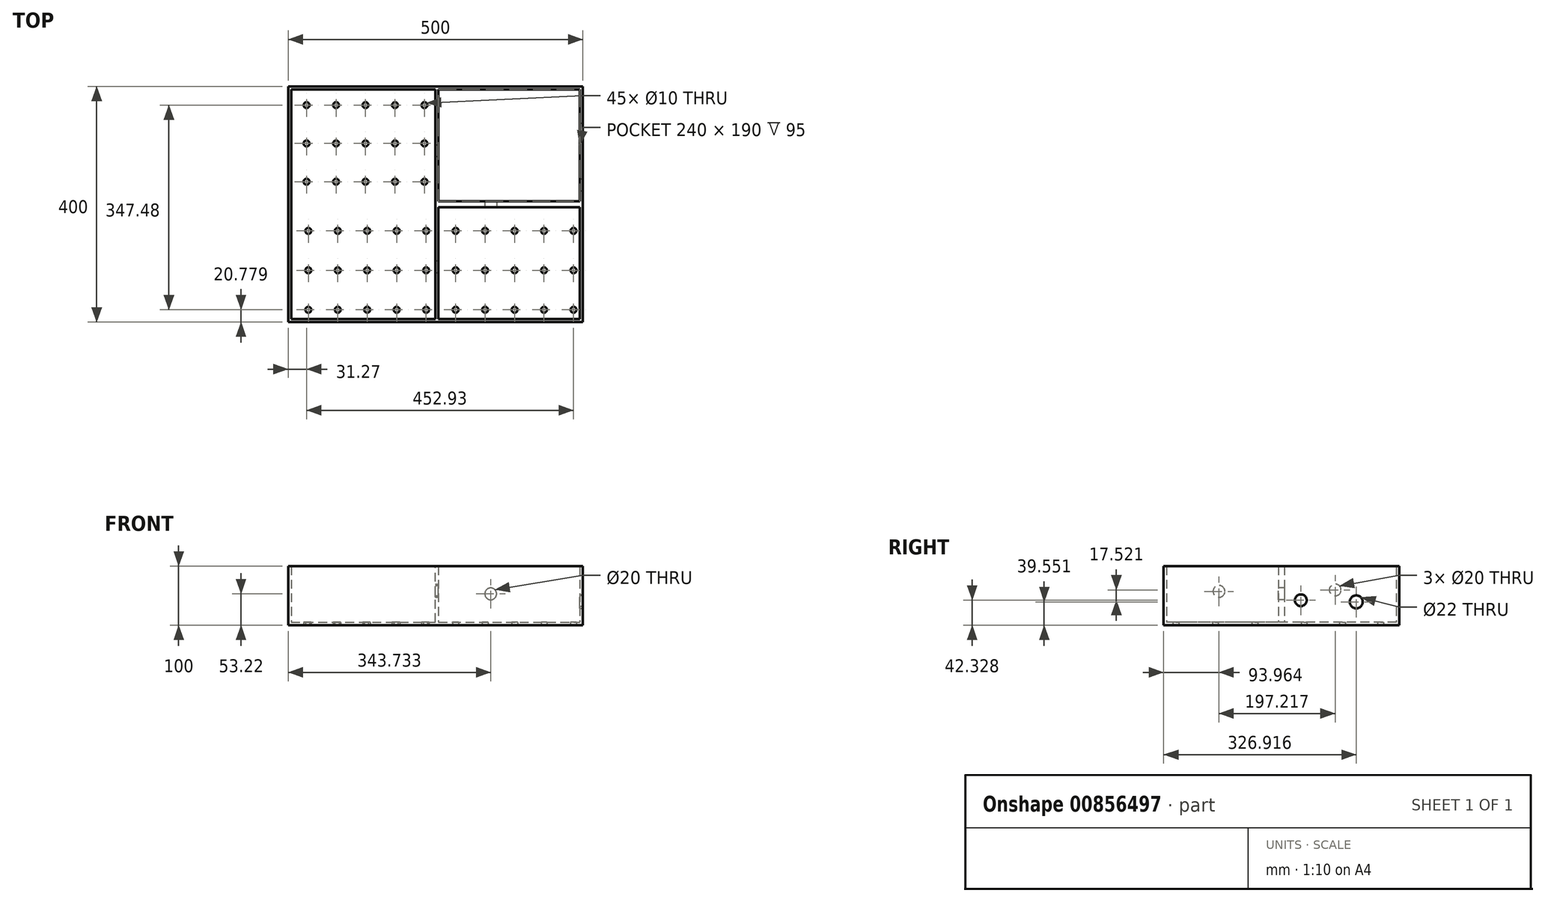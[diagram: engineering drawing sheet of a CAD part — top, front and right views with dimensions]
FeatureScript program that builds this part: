
annotation { "Feature Type Name" : "Feature", "Feature Type Description" : "" }
export const myFeature = defineFeature(function(context is Context, id is Id, definition is map)
    precondition{}
    {
        {
            var Q0;
            Q0=qCreatedBy(makeId("Top.planeOp"),FACE);
            var sketch = newSketch(context, id + "F0", { "sketchPlane" : qUnion([Q0])});
            skLineSegment(sketch, "E0.bottom", {"start": v(0, 0) * mm, "end": v(250, 0) * mm});
            skLineSegment(sketch, "E0.top", {"start": v(0, -400) * mm, "end": v(250, -400) * mm});
            skLineSegment(sketch, "E0.left", {"start": v(0, 0) * mm, "end": v(0, -400) * mm});
            skLineSegment(sketch, "E0.right", {"start": v(250, 0) * mm, "end": v(250, -400) * mm});
            skLineSegment(sketch, "E1.bottom", {"start": v(250, 0) * mm, "end": v(500, 0) * mm});
            skLineSegment(sketch, "E1.top", {"start": v(250, -200) * mm, "end": v(500, -200) * mm});
            skLineSegment(sketch, "E1.left", {"start": v(250, 0) * mm, "end": v(250, -200) * mm});
            skLineSegment(sketch, "E1.right", {"start": v(500, 0) * mm, "end": v(500, -200) * mm});
            skLineSegment(sketch, "E2.top", {"start": v(250, -400) * mm, "end": v(500, -400) * mm});
            skLineSegment(sketch, "E2.left", {"start": v(250, -200) * mm, "end": v(250, -400) * mm});
            skLineSegment(sketch, "E2.right", {"start": v(500, -200) * mm, "end": v(500, -400) * mm});
            skSolve(sketch);
        }
        {
            var Q0;
            {var subQ2=sQuery(id+"F0.wireOp",EDGE,"E1.top");Q0=makeQuery(id+"F0.imprint","IMPRINT",FACE,{"disambiguationData":[TD([[makeQuery(id+"F0.imprint","IMPRINT",EDGE,{"derivedFrom":subQ2}),-1.0]])]});}
            extrude(context, id + "F1", {"entities" : qUnion([Q0]), "depth" : 100 * mm, "offsetDistance" : 25 * mm});
        }
        {
            var Q0;
            Q0=makeQuery(id+"F1.opExtrude","CAP_FACE",FACE,{"disambiguationData":[OSD([sQuery(id+"F0.wireOp",EDGE,"E0.right"),sQuery(id+"F0.wireOp",EDGE,"E1.top"),sQuery(id+"F0.wireOp",EDGE,"E2.top"),sQuery(id+"F0.wireOp",EDGE,"E2.right")])],"isStart":false});
            shell(context, id + "F2", {"entities" : qUnion([Q0]), "thickness" : 5 * mm});
        }
        {
            var Q0;
            {var subQ0=sQuery(id+"F0.wireOp",EDGE,"E1.bottom");Q0=makeQuery(id+"F0.imprint","IMPRINT",FACE,{"disambiguationData":[TD([[makeQuery(id+"F0.imprint","IMPRINT",EDGE,{"derivedFrom":subQ0}),-1.0]])]});}
            extrude(context, id + "F3", {"entities" : qUnion([Q0]), "depth" : 100 * mm, "offsetDistance" : 25 * mm});
        }
        {
            var Q0;
            Q0=makeQuery(id+"F3.opExtrude","CAP_FACE",FACE,{"disambiguationData":[OSD([sQuery(id+"F0.wireOp",EDGE,"E0.right"),sQuery(id+"F0.wireOp",EDGE,"E1.bottom"),sQuery(id+"F0.wireOp",EDGE,"E1.top"),sQuery(id+"F0.wireOp",EDGE,"E1.right")])],"isStart":false});
            shell(context, id + "F4", {"entities" : qUnion([Q0]), "thickness" : 5 * mm});
        }
        {
            var Q0;
            {var subQ3=sQuery(id+"F0.wireOp",EDGE,"E0.bottom");Q0=makeQuery(id+"F0.imprint","IMPRINT",FACE,{"disambiguationData":[TD([[makeQuery(id+"F0.imprint","IMPRINT",EDGE,{"derivedFrom":subQ3}),-1.0]])]});}
            extrude(context, id + "F5", {"entities" : qUnion([Q0]), "operationType" : NewBodyOperationType.ADD, "depth" : 100 * mm, "offsetDistance" : 25 * mm});
        }
        {
            var Q0;
            {var subQ0=sQuery(id+"F0.wireOp",EDGE,"E0.right");var subQ1=sQuery(id+"F0.wireOp",EDGE,"E1.top");Q0=makeQuery(id+"F5.boolean.opBoolean","MERGE",FACE,{"derivedFrom":[makeQuery(id+"F1.opExtrude","CAP_FACE",FACE,{"disambiguationData":[OSD([subQ0,subQ1,sQuery(id+"F0.wireOp",EDGE,"E2.top"),sQuery(id+"F0.wireOp",EDGE,"E2.right")])],"isStart":false}),makeQuery(id+"F3.opExtrude","CAP_FACE",FACE,{"disambiguationData":[OSD([subQ0,sQuery(id+"F0.wireOp",EDGE,"E1.bottom"),subQ1,sQuery(id+"F0.wireOp",EDGE,"E1.right")])],"isStart":false}),makeQuery(id+"F5.opExtrude","CAP_FACE",FACE,{"disambiguationData":[OSD([sQuery(id+"F0.wireOp",EDGE,"E0.bottom"),sQuery(id+"F0.wireOp",EDGE,"E0.top"),sQuery(id+"F0.wireOp",EDGE,"E0.left"),subQ0])],"isStart":false})]});}
            shell(context, id + "F6", {"entities" : qUnion([Q0]), "thickness" : 5 * mm});
        }
        {
            var Q0;
            Q0=makeQuery(id+"F4.opShell","OFFSET_FACE",FACE,{"disambiguationData":[OSD([sQuery(id+"F0.wireOp",EDGE,"E0.right")])]});
            cPlane(context, id + "F7", {"entities" : qUnion([Q0]), "cplaneType" : CPlaneType.OFFSET, "offset" : 0 * mm, "width" : 150 * mm, "height" : 150 * mm});
        }
        {
            var Q0;
            Q0=qCreatedBy(id+"F7.planeOp",FACE);
            var sketch = newSketch(context, id + "F8", { "sketchPlane" : qUnion([Q0])});
            skCircle(sketch, "E3", {"center": v(-108.82, 59.85) * mm, "radius": 10 * mm});
            skCircle(sketch, "E4", {"center": v(-306.04, 57.38) * mm, "radius": 10 * mm});
            skSolve(sketch);
        }
        {
            var Q0;
            Q0 = qSketchRegion(id + "F8", true);
            extrude(context, id + "F9", {"entities" : qUnion([Q0]), "operationType" : NewBodyOperationType.REMOVE, "oppositeDirection" : true, "depth" : 25 * mm, "offsetDistance" : 25 * mm});
        }
        {
            var Q0;
            Q0=makeQuery(id+"F2.opShell","OFFSET_FACE",FACE,{"disambiguationData":[OSD([sQuery(id+"F0.wireOp",EDGE,"E1.top")])]});
            cPlane(context, id + "F10", {"entities" : qUnion([Q0]), "cplaneType" : CPlaneType.OFFSET, "offset" : 0 * mm, "width" : 150 * mm, "height" : 150 * mm});
        }
        {
            var Q0;
            Q0=qCreatedBy(id+"F10.planeOp",FACE);
            var sketch = newSketch(context, id + "F11", { "sketchPlane" : qUnion([Q0])});
            skCircle(sketch, "E5", {"center": v(343.73, 53.22) * mm, "radius": 10 * mm});
            skSolve(sketch);
        }
        {
            var Q0;
            Q0=makeQuery(id+"F11.imprint","IMPRINT",FACE,{"disambiguationData":[TD([[makeQuery(id+"F11.imprint","IMPRINT",EDGE,{"derivedFrom":sQuery(id+"F11.wireOp",EDGE,"E5")}),1.0]])]});
            extrude(context, id + "F12", {"entities" : qUnion([Q0]), "operationType" : NewBodyOperationType.REMOVE, "oppositeDirection" : true, "depth" : 25 * mm, "offsetDistance" : 25 * mm});
        }
        {
            var Q0;
            {var subQ0=sQuery(id+"F0.wireOp",EDGE,"E0.right");var subQ1=sQuery(id+"F0.wireOp",EDGE,"E1.top");Q0=makeQuery(id+"F5.boolean.opBoolean","MERGE",FACE,{"derivedFrom":[makeQuery(id+"F1.opExtrude","CAP_FACE",FACE,{"disambiguationData":[OSD([subQ0,subQ1,sQuery(id+"F0.wireOp",EDGE,"E2.top"),sQuery(id+"F0.wireOp",EDGE,"E2.right")])],"isStart":true}),makeQuery(id+"F3.opExtrude","CAP_FACE",FACE,{"disambiguationData":[OSD([subQ0,sQuery(id+"F0.wireOp",EDGE,"E1.bottom"),subQ1,sQuery(id+"F0.wireOp",EDGE,"E1.right")])],"isStart":true}),makeQuery(id+"F5.opExtrude","CAP_FACE",FACE,{"disambiguationData":[OSD([sQuery(id+"F0.wireOp",EDGE,"E0.bottom"),sQuery(id+"F0.wireOp",EDGE,"E0.top"),sQuery(id+"F0.wireOp",EDGE,"E0.left"),subQ0])],"isStart":true})]});}
            cPlane(context, id + "F13", {"entities" : qUnion([Q0]), "cplaneType" : CPlaneType.OFFSET, "offset" : 0 * mm, "width" : 150 * mm, "height" : 150 * mm});
        }
        {
            var Q0;
            Q0=qCreatedBy(id+"F13.planeOp",FACE);
            var sketch = newSketch(context, id + "F14", { "sketchPlane" : qUnion([Q0])});
            skCircle(sketch, "E6", {"center": v(31.27, 31.74) * mm, "radius": 5 * mm});
            skCircle(sketch, "E7", {"center": v(484.2, 379.22) * mm, "radius": 5 * mm});
            skCircle(sketch, "E8.0.1.0", {"center": v(484.2, 312.22) * mm, "radius": 5 * mm});
            skCircle(sketch, "E8.0.2.0", {"center": v(484.2, 245.22) * mm, "radius": 5 * mm});
            skCircle(sketch, "E8.1.0.0", {"center": v(434.2, 379.22) * mm, "radius": 5 * mm});
            skCircle(sketch, "E8.1.1.0", {"center": v(434.2, 312.22) * mm, "radius": 5 * mm});
            skCircle(sketch, "E8.1.2.0", {"center": v(434.2, 245.22) * mm, "radius": 5 * mm});
            skCircle(sketch, "E8.2.0.0", {"center": v(384.2, 379.22) * mm, "radius": 5 * mm});
            skCircle(sketch, "E8.2.1.0", {"center": v(384.2, 312.22) * mm, "radius": 5 * mm});
            skCircle(sketch, "E8.2.2.0", {"center": v(384.2, 245.22) * mm, "radius": 5 * mm});
            skCircle(sketch, "E8.3.0.0", {"center": v(334.2, 379.22) * mm, "radius": 5 * mm});
            skCircle(sketch, "E8.3.1.0", {"center": v(334.2, 312.22) * mm, "radius": 5 * mm});
            skCircle(sketch, "E8.3.2.0", {"center": v(334.2, 245.22) * mm, "radius": 5 * mm});
            skCircle(sketch, "E8.4.0.0", {"center": v(284.2, 379.22) * mm, "radius": 5 * mm});
            skCircle(sketch, "E8.4.1.0", {"center": v(284.2, 312.22) * mm, "radius": 5 * mm});
            skCircle(sketch, "E8.4.2.0", {"center": v(284.2, 245.22) * mm, "radius": 5 * mm});
            skCircle(sketch, "E8.5.0.0", {"center": v(234.2, 379.22) * mm, "radius": 5 * mm});
            skCircle(sketch, "E8.5.1.0", {"center": v(234.2, 312.22) * mm, "radius": 5 * mm});
            skCircle(sketch, "E8.5.2.0", {"center": v(234.2, 245.22) * mm, "radius": 5 * mm});
            skCircle(sketch, "E8.6.0.0", {"center": v(184.2, 379.22) * mm, "radius": 5 * mm});
            skCircle(sketch, "E8.6.1.0", {"center": v(184.2, 312.22) * mm, "radius": 5 * mm});
            skCircle(sketch, "E8.6.2.0", {"center": v(184.2, 245.22) * mm, "radius": 5 * mm});
            skCircle(sketch, "E8.7.0.0", {"center": v(134.2, 379.22) * mm, "radius": 5 * mm});
            skCircle(sketch, "E8.7.1.0", {"center": v(134.2, 312.22) * mm, "radius": 5 * mm});
            skCircle(sketch, "E8.7.2.0", {"center": v(134.2, 245.22) * mm, "radius": 5 * mm});
            skCircle(sketch, "E8.8.0.0", {"center": v(84.2, 379.22) * mm, "radius": 5 * mm});
            skCircle(sketch, "E8.8.1.0", {"center": v(84.2, 312.22) * mm, "radius": 5 * mm});
            skCircle(sketch, "E8.8.2.0", {"center": v(84.2, 245.22) * mm, "radius": 5 * mm});
            skCircle(sketch, "E8.9.0.0", {"center": v(34.2, 379.22) * mm, "radius": 5 * mm});
            skCircle(sketch, "E8.9.1.0", {"center": v(34.2, 312.22) * mm, "radius": 5 * mm});
            skCircle(sketch, "E8.9.2.0", {"center": v(34.2, 245.22) * mm, "radius": 5 * mm});
            skLineSegment(sketch, "E8.direction1", {"start": v(484.2, 379.22) * mm, "end": v(434.2, 379.22) * mm, "construction": true});
            skLineSegment(sketch, "E8.direction2", {"start": v(484.2, 379.22) * mm, "end": v(484.2, 312.22) * mm, "construction": true});
            skCircle(sketch, "E9.0.1.0", {"center": v(31.27, 96.74) * mm, "radius": 5 * mm});
            skCircle(sketch, "E9.0.2.0", {"center": v(31.27, 161.74) * mm, "radius": 5 * mm});
            skCircle(sketch, "E9.1.0.0", {"center": v(81.27, 31.74) * mm, "radius": 5 * mm});
            skCircle(sketch, "E9.1.1.0", {"center": v(81.27, 96.74) * mm, "radius": 5 * mm});
            skCircle(sketch, "E9.1.2.0", {"center": v(81.27, 161.74) * mm, "radius": 5 * mm});
            skCircle(sketch, "E9.2.0.0", {"center": v(131.27, 31.74) * mm, "radius": 5 * mm});
            skCircle(sketch, "E9.2.1.0", {"center": v(131.27, 96.74) * mm, "radius": 5 * mm});
            skCircle(sketch, "E9.2.2.0", {"center": v(131.27, 161.74) * mm, "radius": 5 * mm});
            skCircle(sketch, "E9.3.0.0", {"center": v(181.27, 31.74) * mm, "radius": 5 * mm});
            skCircle(sketch, "E9.3.1.0", {"center": v(181.27, 96.74) * mm, "radius": 5 * mm});
            skCircle(sketch, "E9.3.2.0", {"center": v(181.27, 161.74) * mm, "radius": 5 * mm});
            skCircle(sketch, "E9.4.0.0", {"center": v(231.27, 31.74) * mm, "radius": 5 * mm});
            skCircle(sketch, "E9.4.1.0", {"center": v(231.27, 96.74) * mm, "radius": 5 * mm});
            skCircle(sketch, "E9.4.2.0", {"center": v(231.27, 161.74) * mm, "radius": 5 * mm});
            skLineSegment(sketch, "E9.direction1", {"start": v(31.27, 31.74) * mm, "end": v(81.27, 31.74) * mm, "construction": true});
            skLineSegment(sketch, "E9.direction2", {"start": v(31.27, 31.74) * mm, "end": v(31.27, 96.74) * mm, "construction": true});
            skSolve(sketch);
        }
        {
            var Q0;
            Q0 = qSketchRegion(id + "F14", true);
            extrude(context, id + "F15", {"entities" : qUnion([Q0]), "operationType" : NewBodyOperationType.REMOVE, "oppositeDirection" : true, "depth" : 25 * mm, "offsetDistance" : 25 * mm});
        }
        {
            var Q0;
            Q0=makeQuery(id+"F5.boolean.opBoolean","MERGE",FACE,{"derivedFrom":[makeQuery(id+"F1.opExtrude","SWEPT_FACE",FACE,{"disambiguationData":[OSD([sQuery(id+"F0.wireOp",EDGE,"E2.right")])]}),makeQuery(id+"F3.opExtrude","SWEPT_FACE",FACE,{"disambiguationData":[OSD([sQuery(id+"F0.wireOp",EDGE,"E1.right")])]})]});
            cPlane(context, id + "F16", {"entities" : qUnion([Q0]), "cplaneType" : CPlaneType.OFFSET, "offset" : 0 * mm, "width" : 150 * mm, "height" : 150 * mm});
        }
        {
            var Q0;
            Q0=qCreatedBy(id+"F16.planeOp",FACE);
            var sketch = newSketch(context, id + "F17", { "sketchPlane" : qUnion([Q0])});
            skCircle(sketch, "E10", {"center": v(-167.15, 42.33) * mm, "radius": 10 * mm});
            skSolve(sketch);
        }
        {
            var Q0;
            Q0=makeQuery(id+"F17.imprint","IMPRINT",FACE,{"disambiguationData":[TD([[makeQuery(id+"F17.imprint","IMPRINT",EDGE,{"derivedFrom":sQuery(id+"F17.wireOp",EDGE,"E10")}),1.0]])]});
            extrude(context, id + "F18", {"entities" : qUnion([Q0]), "operationType" : NewBodyOperationType.REMOVE, "oppositeDirection" : true, "depth" : 25 * mm, "offsetDistance" : 25 * mm});
        }
        {
            var Q0;
            Q0=qCreatedBy(id+"F16.planeOp",FACE);
            var sketch = newSketch(context, id + "F19", { "sketchPlane" : qUnion([Q0])});
            skCircle(sketch, "E11", {"center": v(-73.08, 39.55) * mm, "radius": 11 * mm});
            skSolve(sketch);
        }
        {
            var Q0;
            Q0 = qSketchRegion(id + "F19", true);
            extrude(context, id + "F20", {"entities" : qUnion([Q0]), "operationType" : NewBodyOperationType.REMOVE, "oppositeDirection" : true, "depth" : 25 * mm, "offsetDistance" : 25 * mm});
        }
    });
